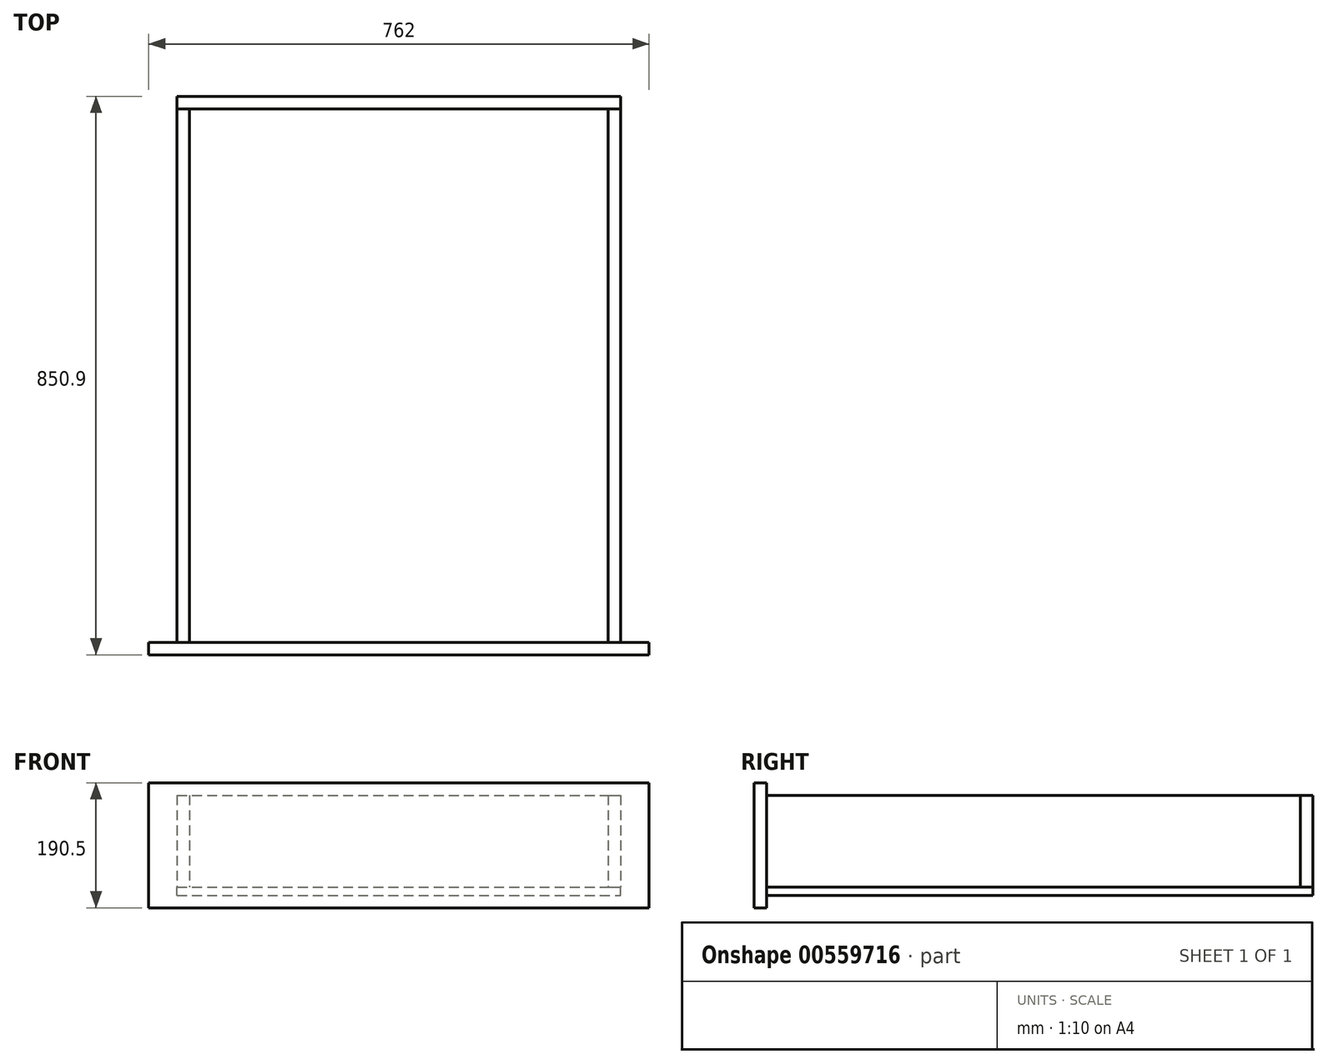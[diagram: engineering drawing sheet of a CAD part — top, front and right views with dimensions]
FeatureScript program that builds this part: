
annotation { "Feature Type Name" : "Feature", "Feature Type Description" : "" }
export const myFeature = defineFeature(function(context is Context, id is Id, definition is map)
    precondition{}
    {
        {
            var Q0;
            Q0=qCreatedBy(makeId("Top.planeOp"),FACE);
            var sketch = newSketch(context, id + "F0", { "sketchPlane" : qUnion([Q0])});
            skLineSegment(sketch, "E0.bottom", {"start": v(318.77, 812.8) * mm, "end": v(337.82, 812.8) * mm});
            skLineSegment(sketch, "E0.top", {"start": v(318.77, 0) * mm, "end": v(337.82, 0) * mm});
            skLineSegment(sketch, "E0.left", {"start": v(318.77, 812.8) * mm, "end": v(318.77, 0) * mm});
            skLineSegment(sketch, "E0.right", {"start": v(337.82, 812.8) * mm, "end": v(337.82, 0) * mm});
            skLineSegment(sketch, "E1.bottom", {"start": v(-337.82, 812.8) * mm, "end": v(-318.77, 812.8) * mm});
            skLineSegment(sketch, "E1.top", {"start": v(-337.82, 0) * mm, "end": v(-318.77, 0) * mm});
            skLineSegment(sketch, "E1.left", {"start": v(-337.82, 812.8) * mm, "end": v(-337.82, 0) * mm});
            skLineSegment(sketch, "E1.right", {"start": v(-318.77, 812.8) * mm, "end": v(-318.77, 0) * mm});
            skLineSegment(sketch, "E2", {"start": v(318.77, 0) * mm, "end": v(0, 0) * mm, "construction": true});
            skLineSegment(sketch, "E3", {"start": v(0, 0) * mm, "end": v(-318.77, 0) * mm, "construction": true});
            skSolve(sketch);
        }
        {
            var Q0;
            Q0 = qSketchRegion(id + "F0", true);
            extrude(context, id + "F1", {"entities" : qUnion([Q0]), "depth" : 139.7 * mm, "offsetDistance" : 25.4 * mm});
        }
        {
            var Q0;
            Q0=qCreatedBy(makeId("Top.planeOp"),FACE);
            var sketch = newSketch(context, id + "F2", { "sketchPlane" : qUnion([Q0])});
            skLineSegment(sketch, "E4.bottom", {"start": v(-337.82, 812.8) * mm, "end": v(337.82, 812.8) * mm});
            skLineSegment(sketch, "E4.top", {"start": v(-337.82, 831.85) * mm, "end": v(337.82, 831.85) * mm});
            skLineSegment(sketch, "E4.left", {"start": v(-337.82, 812.8) * mm, "end": v(-337.82, 831.85) * mm});
            skLineSegment(sketch, "E4.right", {"start": v(337.82, 812.8) * mm, "end": v(337.82, 831.85) * mm});
            skSolve(sketch);
        }
        {
            var Q0;
            Q0 = qSketchRegion(id + "F2", true);
            extrude(context, id + "F3", {"entities" : qUnion([Q0]), "depth" : 139.7 * mm, "offsetDistance" : 25.4 * mm});
        }
        {
            var Q0;
            Q0=qCreatedBy(makeId("Top.planeOp"),FACE);
            var sketch = newSketch(context, id + "F4", { "sketchPlane" : qUnion([Q0])});
            skLineSegment(sketch, "E5.bottom", {"start": v(-337.82, 0) * mm, "end": v(337.82, 0) * mm});
            skLineSegment(sketch, "E5.top", {"start": v(-337.82, 831.85) * mm, "end": v(337.82, 831.85) * mm});
            skLineSegment(sketch, "E5.left", {"start": v(-337.82, 0) * mm, "end": v(-337.82, 831.85) * mm});
            skLineSegment(sketch, "E5.right", {"start": v(337.82, 0) * mm, "end": v(337.82, 831.85) * mm});
            skSolve(sketch);
        }
        {
            var Q0;
            Q0 = qSketchRegion(id + "F4", true);
            extrude(context, id + "F5", {"entities" : qUnion([Q0]), "oppositeDirection" : true, "depth" : 12.7 * mm, "offsetDistance" : 25.4 * mm});
        }
        {
            var Q0;
            Q0=qCreatedBy(makeId("Front.planeOp"),FACE);
            var sketch = newSketch(context, id + "F6", { "sketchPlane" : qUnion([Q0])});
            skLineSegment(sketch, "E6.bottom", {"start": v(-381, 158.75) * mm, "end": v(381, 158.75) * mm});
            skLineSegment(sketch, "E6.top", {"start": v(-381, -31.75) * mm, "end": v(381, -31.75) * mm});
            skLineSegment(sketch, "E6.left", {"start": v(-381, 158.75) * mm, "end": v(-381, -31.75) * mm});
            skLineSegment(sketch, "E6.right", {"start": v(381, 158.75) * mm, "end": v(381, -31.75) * mm});
            skLineSegment(sketch, "E7", {"start": v(0, -31.75) * mm, "end": v(0, 0) * mm, "construction": true});
            skLineSegment(sketch, "E8", {"start": v(0, 139.7) * mm, "end": v(0, 158.75) * mm, "construction": true});
            skLineSegment(sketch, "E9", {"start": v(25.57, -31.75) * mm, "end": v(25.57, -12.7) * mm, "construction": true});
            skSolve(sketch);
        }
        {
            var Q0;
            Q0=makeQuery(id+"F6.imprint","IMPRINT",FACE,{"disambiguationData":[TD([[makeQuery(id+"F6.imprint","IMPRINT",EDGE,{"derivedFrom":sQuery(id+"F6.wireOp",EDGE,"E6.bottom")}),-1.0]])]});
            var Q1;
            Q1 = qConstructionFilter(qBodyType(qCreatedBy(id + "F6" ,EDGE), BodyType.WIRE), ConstructionObject.NO);
            extrude(context, id + "F7", {"entities" : qUnion([Q0]), "surfaceEntities" : qUnion([Q1]), "depth" : 19.05 * mm, "offsetDistance" : 25.4 * mm});
        }
    });
